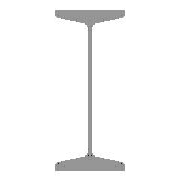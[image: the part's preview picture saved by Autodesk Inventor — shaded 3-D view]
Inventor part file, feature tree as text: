
AUTODESK INVENTOR PART (.ipt)
format: ipt  version: 2025 (Build 290162010, 162A)  size: 146,432 bytes
history: native  units: mm (DEFAULTED — no unit token found)
features: other x3, sketch x1, plane x1
ambient origin geometry x8: Origin, YZ Plane, XZ Plane, XY Plane, X Axis, Y Axis, Z Axis, Center Point
bodies: Solid1 (feature_tree), Body (feature_tree)
feature tree (5):
  other  "Driven Length"
  other  "Start plane"
  other  "End plane"
  sketch  "Sketch3"  dims[d1=2.266221mm d2=8.4mm d3=16.125mm d4=2.75mm d5=35.0mm d6=3000.0mm d7=0.0mm d10=70.0mm d14=4.0mm d15=8.0mm d16=-0.0mm d17=3000.0mm d18=90.0deg d19=3000.0mm]
  plane  "Work Plane3"
